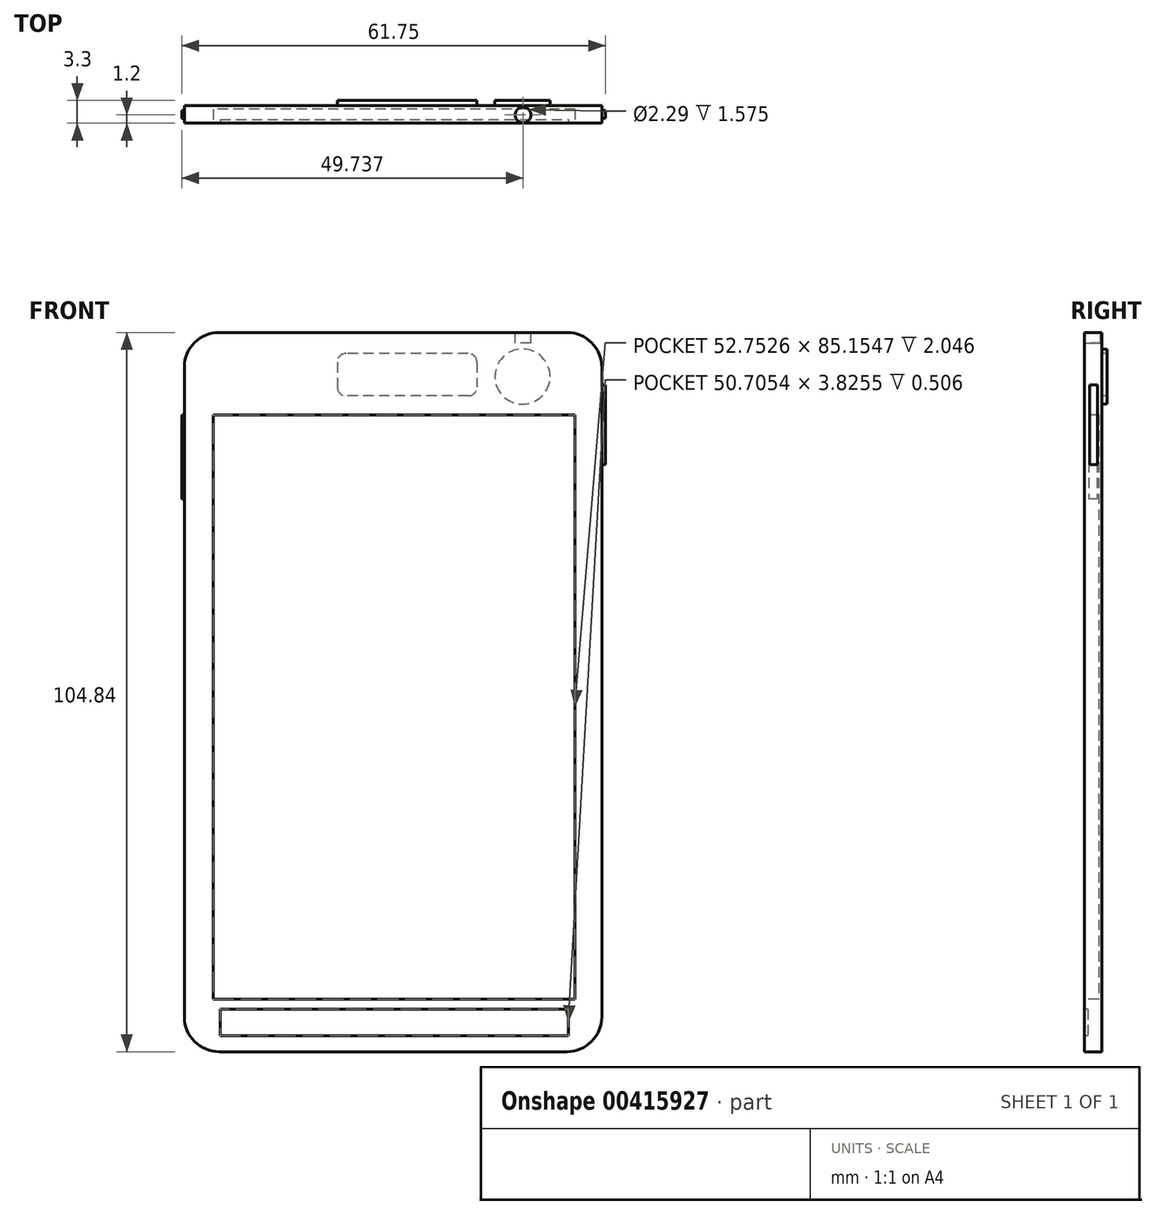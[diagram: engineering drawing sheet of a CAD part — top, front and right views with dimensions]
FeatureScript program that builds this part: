
annotation { "Feature Type Name" : "Feature", "Feature Type Description" : "" }
export const myFeature = defineFeature(function(context is Context, id is Id, definition is map)
    precondition{}
    {
        {
            var Q0;
            Q0=qCreatedBy(makeId("Front.planeOp"),FACE);
            var sketch = newSketch(context, id + "F0", { "sketchPlane" : qUnion([Q0])});
            skLineSegment(sketch, "E0.bottom", {"start": v(-30.56, 49.3) * mm, "end": v(30.26, 49.3) * mm});
            skLineSegment(sketch, "E0.top", {"start": v(-30.56, -55.54) * mm, "end": v(30.26, -55.54) * mm});
            skLineSegment(sketch, "E0.left", {"start": v(-30.56, 49.3) * mm, "end": v(-30.56, -55.54) * mm});
            skLineSegment(sketch, "E0.right", {"start": v(30.26, 49.3) * mm, "end": v(30.26, -55.54) * mm});
            skSolve(sketch);
        }
        {
            var Q0;
            Q0=makeQuery(id+"F0.imprint","IMPRINT",FACE,{"disambiguationData":[TD([[makeQuery(id+"F0.imprint","IMPRINT",EDGE,{"derivedFrom":sQuery(id+"F0.wireOp",EDGE,"E0.bottom")}),-1.0]])]});
            extrude(context, id + "F1", {"entities" : qUnion([Q0]), "depth" : 2.54 * mm});
        }
        {
            var Q0;
            Q0=makeQuery(id+"F1.opExtrude","SWEPT_EDGE",EDGE,{"disambiguationData":[OSD([sQuery(id+"F0.wireOp",EDGE,"E0.top"),sQuery(id+"F0.wireOp",EDGE,"E0.right")])]});
            fillet(context, id + "F2", {"entities" : qUnion([Q0]), "radius" : 5.08 * mm, "tangentPropagation" : true, "allowEdgeOverflow" : false});
        }
        {
            var Q0;
            Q0=makeQuery(id+"F1.opExtrude","SWEPT_EDGE",EDGE,{"disambiguationData":[OSD([sQuery(id+"F0.wireOp",EDGE,"E0.top"),sQuery(id+"F0.wireOp",EDGE,"E0.left")])]});
            fillet(context, id + "F3", {"entities" : qUnion([Q0]), "radius" : 5.08 * mm, "tangentPropagation" : true, "allowEdgeOverflow" : false});
        }
        {
            var Q0;
            Q0=makeQuery(id+"F1.opExtrude","SWEPT_EDGE",EDGE,{"disambiguationData":[OSD([sQuery(id+"F0.wireOp",EDGE,"E0.bottom"),sQuery(id+"F0.wireOp",EDGE,"E0.left")])]});
            fillet(context, id + "F4", {"entities" : qUnion([Q0]), "radius" : 5.08 * mm, "tangentPropagation" : true, "allowEdgeOverflow" : false});
        }
        {
            var Q0;
            Q0=makeQuery(id+"F1.opExtrude","SWEPT_EDGE",EDGE,{"disambiguationData":[OSD([sQuery(id+"F0.wireOp",EDGE,"E0.bottom"),sQuery(id+"F0.wireOp",EDGE,"E0.right")])]});
            fillet(context, id + "F5", {"entities" : qUnion([Q0]), "radius" : 5.08 * mm, "tangentPropagation" : true, "allowEdgeOverflow" : false});
        }
        {
            var Q0;
            Q0=makeQuery(id+"F1.opExtrude","CAP_FACE",FACE,{"disambiguationData":[OSD([sQuery(id+"F0.wireOp",EDGE,"E0.bottom"),sQuery(id+"F0.wireOp",EDGE,"E0.top"),sQuery(id+"F0.wireOp",EDGE,"E0.left"),sQuery(id+"F0.wireOp",EDGE,"E0.right")])],"isStart":true});
            var sketch = newSketch(context, id + "F6", { "sketchPlane" : qUnion([Q0])});
            skCircle(sketch, "E1", {"center": v(-18.7, 42.87) * mm, "radius": 4.02 * mm});
            skSolve(sketch);
        }
        {
            var Q0;
            Q0=makeQuery(id+"F6.imprint","IMPRINT",FACE,{"disambiguationData":[TD([[makeQuery(id+"F6.imprint","IMPRINT",EDGE,{"derivedFrom":sQuery(id+"F6.wireOp",EDGE,"E1")}),1.0]])]});
            extrude(context, id + "F7", {"entities" : qUnion([Q0]), "operationType" : NewBodyOperationType.ADD, "depth" : 0.76 * mm});
        }
        {
            var Q0;
            Q0=makeQuery(id+"F1.opExtrude","CAP_FACE",FACE,{"disambiguationData":[OSD([sQuery(id+"F0.wireOp",EDGE,"E0.bottom"),sQuery(id+"F0.wireOp",EDGE,"E0.top"),sQuery(id+"F0.wireOp",EDGE,"E0.left"),sQuery(id+"F0.wireOp",EDGE,"E0.right")])],"isStart":true});
            var sketch = newSketch(context, id + "F8", { "sketchPlane" : qUnion([Q0])});
            skLineSegment(sketch, "E2.bottom", {"start": v(-12.07, 46.23) * mm, "end": v(8.28, 46.23) * mm});
            skLineSegment(sketch, "E2.top", {"start": v(-12.07, 40.05) * mm, "end": v(8.28, 40.05) * mm});
            skLineSegment(sketch, "E2.left", {"start": v(-12.07, 46.23) * mm, "end": v(-12.07, 40.05) * mm});
            skLineSegment(sketch, "E2.right", {"start": v(8.28, 46.23) * mm, "end": v(8.28, 40.05) * mm});
            skSolve(sketch);
        }
        {
            var Q0;
            Q0=makeQuery(id+"F8.imprint","IMPRINT",FACE,{"disambiguationData":[TD([[makeQuery(id+"F8.imprint","IMPRINT",EDGE,{"derivedFrom":sQuery(id+"F8.wireOp",EDGE,"E2.bottom")}),-1.0]])]});
            extrude(context, id + "F9", {"entities" : qUnion([Q0]), "operationType" : NewBodyOperationType.ADD, "depth" : 0.76 * mm});
        }
        {
            var Q0;
            Q0=makeQuery(id+"F9.opExtrude","SWEPT_EDGE",EDGE,{"disambiguationData":[OSD([sQuery(id+"F8.wireOp",EDGE,"E2.bottom"),sQuery(id+"F8.wireOp",EDGE,"E2.right")])]});
            var Q1;
            Q1=makeQuery(id+"F9.opExtrude","SWEPT_EDGE",EDGE,{"disambiguationData":[OSD([sQuery(id+"F8.wireOp",EDGE,"E2.top"),sQuery(id+"F8.wireOp",EDGE,"E2.right")])]});
            var Q2;
            Q2=makeQuery(id+"F9.opExtrude","SWEPT_EDGE",EDGE,{"disambiguationData":[OSD([sQuery(id+"F8.wireOp",EDGE,"E2.top"),sQuery(id+"F8.wireOp",EDGE,"E2.left")])]});
            var Q3;
            Q3=makeQuery(id+"F9.opExtrude","SWEPT_EDGE",EDGE,{"disambiguationData":[OSD([sQuery(id+"F8.wireOp",EDGE,"E2.bottom"),sQuery(id+"F8.wireOp",EDGE,"E2.left")])]});
            fillet(context, id + "F10", {"entities" : qUnion([Q0, Q1, Q2, Q3]), "radius" : 1.27 * mm, "tangentPropagation" : true, "allowEdgeOverflow" : false});
        }
        {
            var Q0;
            Q0=makeQuery(id+"F1.opExtrude","CAP_FACE",FACE,{"disambiguationData":[OSD([sQuery(id+"F0.wireOp",EDGE,"E0.bottom"),sQuery(id+"F0.wireOp",EDGE,"E0.top"),sQuery(id+"F0.wireOp",EDGE,"E0.left"),sQuery(id+"F0.wireOp",EDGE,"E0.right")])],"isStart":false});
            var sketch = newSketch(context, id + "F11", { "sketchPlane" : qUnion([Q0])});
            skLineSegment(sketch, "E3.bottom", {"start": v(26.38, 37.29) * mm, "end": v(-26.38, 37.29) * mm});
            skLineSegment(sketch, "E3.top", {"start": v(26.38, -47.87) * mm, "end": v(-26.38, -47.87) * mm});
            skLineSegment(sketch, "E3.left", {"start": v(26.38, 37.29) * mm, "end": v(26.38, -47.87) * mm});
            skLineSegment(sketch, "E3.right", {"start": v(-26.38, 37.29) * mm, "end": v(-26.38, -47.87) * mm});
            skPoint(sketch, "E3.middle", {"position": v(0, -5.29) * mm});
            skSolve(sketch);
        }
        {
            var Q0;
            Q0=makeQuery(id+"F11.imprint","IMPRINT",FACE,{"disambiguationData":[TD([[makeQuery(id+"F11.imprint","IMPRINT",EDGE,{"derivedFrom":sQuery(id+"F11.wireOp",EDGE,"E3.bottom")}),1.0]])]});
            extrude(context, id + "F12", {"entities" : qUnion([Q0]), "operationType" : NewBodyOperationType.REMOVE, "oppositeDirection" : true, "depth" : 2.05 * mm});
        }
        {
            var Q0;
            Q0=makeQuery(id+"F1.opExtrude","CAP_FACE",FACE,{"disambiguationData":[OSD([sQuery(id+"F0.wireOp",EDGE,"E0.bottom"),sQuery(id+"F0.wireOp",EDGE,"E0.top"),sQuery(id+"F0.wireOp",EDGE,"E0.left"),sQuery(id+"F0.wireOp",EDGE,"E0.right")])],"isStart":false});
            var sketch = newSketch(context, id + "F13", { "sketchPlane" : qUnion([Q0])});
            skLineSegment(sketch, "E4.bottom", {"start": v(-25.34, -49.36) * mm, "end": v(25.37, -49.36) * mm});
            skLineSegment(sketch, "E4.top", {"start": v(-25.34, -53.18) * mm, "end": v(25.37, -53.18) * mm});
            skLineSegment(sketch, "E4.left", {"start": v(-25.34, -49.36) * mm, "end": v(-25.34, -53.18) * mm});
            skLineSegment(sketch, "E4.right", {"start": v(25.37, -49.36) * mm, "end": v(25.37, -53.18) * mm});
            skSolve(sketch);
        }
        {
            var Q0;
            Q0=makeQuery(id+"F13.imprint","IMPRINT",FACE,{"disambiguationData":[TD([[makeQuery(id+"F13.imprint","IMPRINT",EDGE,{"derivedFrom":sQuery(id+"F13.wireOp",EDGE,"E4.bottom")}),-1.0]])]});
            extrude(context, id + "F14", {"entities" : qUnion([Q0]), "operationType" : NewBodyOperationType.REMOVE, "oppositeDirection" : true, "depth" : 0.5 * mm});
        }
        {
            var Q0;
            Q0=makeQuery(id+"F1.opExtrude","SWEPT_FACE",FACE,{"disambiguationData":[OSD([sQuery(id+"F0.wireOp",EDGE,"E0.bottom")])]});
            var sketch = newSketch(context, id + "F15", { "sketchPlane" : qUnion([Q0])});
            skSolve(sketch);
        }
        {
            var Q0;
            {var subQ0=sQuery(id+"F0.wireOp",EDGE,"E0.bottom");Q0=makeQuery(id+"F15.imprint","IMPRINT",FACE,{"disambiguationData":[TD([[makeQuery(id+"F15.imprint","IMPRINT",EDGE,{"derivedFrom":makeQuery(id+"F1.opExtrude","CAP_EDGE",EDGE,{"disambiguationData":[OSD([subQ0])],"isStart":true})}),-1.0]])]});}
            var sketch = newSketch(context, id + "F16", { "sketchPlane" : qUnion([Q0])});
            skCircle(sketch, "E5", {"center": v(18.79, -1.34) * mm, "radius": 1.15 * mm});
            skSolve(sketch);
        }
        {
            var Q0;
            Q0=makeQuery(id+"F16.imprint","IMPRINT",FACE,{"disambiguationData":[TD([[makeQuery(id+"F16.imprint","IMPRINT",EDGE,{"derivedFrom":sQuery(id+"F16.wireOp",EDGE,"E5")}),1.0]])]});
            extrude(context, id + "F17", {"entities" : qUnion([Q0]), "operationType" : NewBodyOperationType.REMOVE, "oppositeDirection" : true, "depth" : 1.57 * mm});
        }
        {
            var Q0;
            Q0=makeQuery(id+"F1.opExtrude","SWEPT_FACE",FACE,{"disambiguationData":[OSD([sQuery(id+"F0.wireOp",EDGE,"E0.left")])]});
            var sketch = newSketch(context, id + "F18", { "sketchPlane" : qUnion([Q0])});
            skLineSegment(sketch, "E6.bottom", {"start": v(0.65, 41.59) * mm, "end": v(1.86, 41.59) * mm});
            skLineSegment(sketch, "E6.top", {"start": v(0.65, 30) * mm, "end": v(1.86, 30) * mm});
            skLineSegment(sketch, "E6.left", {"start": v(0.65, 41.59) * mm, "end": v(0.65, 30) * mm});
            skLineSegment(sketch, "E6.right", {"start": v(1.86, 41.59) * mm, "end": v(1.86, 30) * mm});
            skSolve(sketch);
        }
        {
            var Q0;
            Q0=makeQuery(id+"F18.imprint","IMPRINT",FACE,{"disambiguationData":[TD([[makeQuery(id+"F18.imprint","IMPRINT",EDGE,{"derivedFrom":sQuery(id+"F18.wireOp",EDGE,"E6.bottom")}),1.0]])]});
            var sketch = newSketch(context, id + "F19", { "sketchPlane" : qUnion([Q0])});
            skLineSegment(sketch, "E7.bottom", {"start": v(0.71, 37.3) * mm, "end": v(1.9, 37.3) * mm});
            skLineSegment(sketch, "E7.top", {"start": v(0.71, 25) * mm, "end": v(1.9, 25) * mm});
            skLineSegment(sketch, "E7.left", {"start": v(0.71, 37.3) * mm, "end": v(0.71, 25) * mm});
            skLineSegment(sketch, "E7.right", {"start": v(1.9, 37.3) * mm, "end": v(1.9, 25) * mm});
            skSolve(sketch);
        }
        {
            var Q0;
            Q0 = qSketchRegion(id + "F19", true);
            extrude(context, id + "F20", {"entities" : qUnion([Q0]), "operationType" : NewBodyOperationType.ADD, "depth" : 0.38 * mm});
        }
        {
            var Q0;
            Q0=makeQuery(id+"F1.opExtrude","SWEPT_FACE",FACE,{"disambiguationData":[OSD([sQuery(id+"F0.wireOp",EDGE,"E0.right")])]});
            var sketch = newSketch(context, id + "F21", { "sketchPlane" : qUnion([Q0])});
            skLineSegment(sketch, "E8.bottom", {"start": v(-1.8, 41.67) * mm, "end": v(-0.66, 41.67) * mm});
            skLineSegment(sketch, "E8.top", {"start": v(-1.8, 30.05) * mm, "end": v(-0.66, 30.05) * mm});
            skLineSegment(sketch, "E8.left", {"start": v(-1.8, 41.67) * mm, "end": v(-1.8, 30.05) * mm});
            skLineSegment(sketch, "E8.right", {"start": v(-0.66, 41.67) * mm, "end": v(-0.66, 30.05) * mm});
            skSolve(sketch);
        }
        {
            var Q0;
            Q0=makeQuery(id+"F21.imprint","IMPRINT",FACE,{"disambiguationData":[TD([[makeQuery(id+"F21.imprint","IMPRINT",EDGE,{"derivedFrom":sQuery(id+"F21.wireOp",EDGE,"E8.bottom")}),-1.0]])]});
            extrude(context, id + "F22", {"entities" : qUnion([Q0]), "operationType" : NewBodyOperationType.ADD, "depth" : 0.54 * mm});
        }
    });
